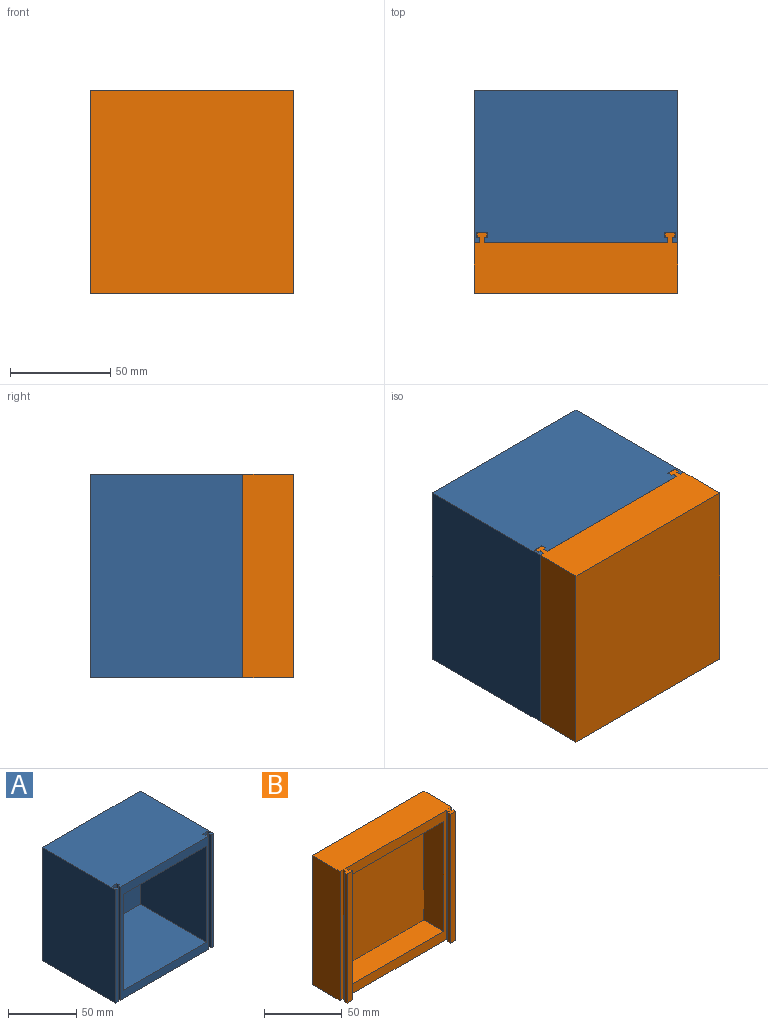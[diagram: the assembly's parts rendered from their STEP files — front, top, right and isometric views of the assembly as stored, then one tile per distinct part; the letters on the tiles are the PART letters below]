
ASSEMBLY  parts=2 mates=1
PART A: 27 faces, bbox 101.6x76.2x101.6 mm
  f0: plane 101.6x91.44mm, normal (0,-1,0), area 1832.3mm2, adj f2,f3,f8,f9,f10,f11,f13,f26
  f1: plane 101.6x2.54mm, normal (0,-1,0), area 258.1mm2, adj f2,f3,f5,f19
  f2: plane 101.6x76.2mm, normal (0,0,-1), area 7703.2mm2, adj f0,f1,f4,f5,f6,f7,f13,f14
  f3: plane 101.6x76.2mm, normal (0,0,1), area 7703.2mm2, adj f0,f1,f4,f5,f6,f7,f13,f14
  f4: plane 101.6x2.54mm, normal (0,-1,0), area 258.1mm2, adj f2,f3,f6,f20
  f5: plane 101.6x76.2mm, normal (1,0,0), area 7741.9mm2, adj f1,f2,f3,f7
  f6: plane 101.6x76.2mm, normal (-1,0,0), area 7741.9mm2, adj f2,f3,f4,f7
  f7: plane 101.6x101.6mm, normal (0,1,0), area 10322.6mm2, adj f2,f3,f5,f6
  f8: plane 86.36x68.58mm, normal (0,0,1), area 5922.6mm2, adj f0,f9,f11,f12
  f9: plane 86.36x68.58mm, normal (-1,0,0), area 5922.6mm2, adj f0,f8,f10,f12
  f10: plane 86.36x68.58mm, normal (0,0,-1), area 5922.6mm2, adj f0,f9,f11,f12
  f11: plane 86.36x68.58mm, normal (1,0,0), area 5922.6mm2, adj f0,f8,f10,f12
  f12: plane 86.36x86.36mm, normal (0,-1,0), area 7458mm2, adj f8,f9,f10,f11
  f13: plane 101.6x2.54mm, normal (1,0,0), area 258.1mm2, adj f0,f2,f3,f14
  f14: plane 101.6x1.27mm, normal (0,1,0), area 129mm2, adj f2,f3,f13,f15
  f15: plane 101.6x2.54mm, normal (1,0,0), area 258.1mm2, adj f2,f3,f14,f16
  f16: plane 101.6x5.08mm, normal (0,-1,0), area 516.1mm2, adj f2,f3,f15,f17
  f17: plane 101.6x2.54mm, normal (-1,0,0), area 258.1mm2, adj f2,f3,f16,f18
  f18: plane 101.6x1.27mm, normal (0,1,0), area 129mm2, adj f2,f3,f17,f19
  f19: plane 101.6x2.54mm, normal (-1,0,0), area 258.1mm2, adj f1,f2,f3,f18
  f20: plane 101.6x2.54mm, normal (1,0,0), area 258.1mm2, adj f2,f3,f4,f21
  f21: plane 101.6x1.27mm, normal (0,1,0), area 129mm2, adj f2,f3,f20,f22
  f22: plane 101.6x2.54mm, normal (1,0,0), area 258.1mm2, adj f2,f3,f21,f23
  f23: plane 101.6x5.08mm, normal (0,-1,0), area 516.1mm2, adj f2,f3,f22,f24
  f24: plane 101.6x2.54mm, normal (-1,0,0), area 258.1mm2, adj f2,f3,f23,f25
  f25: plane 101.6x1.27mm, normal (0,1,0), area 129mm2, adj f2,f3,f24,f26
  f26: plane 101.6x2.54mm, normal (-1,0,0), area 258.1mm2, adj f0,f2,f3,f25
PART B: 27 faces, bbox 101.6x30.4x101.6 mm
  f0: plane 101.6x2.67mm, normal (0,-1,0), area 271mm2, adj f3,f4,f5,f20
  f1: plane 101.6x91.69mm, normal (0,-1,0), area 1858.1mm2, adj f3,f5,f8,f9,f10,f11,f14,f26
  f2: plane 101.6x2.67mm, normal (0,-1,0), area 271mm2, adj f3,f5,f6,f13
  f3: plane 101.6x30.35mm, normal (0,0,-1), area 2614.9mm2, adj f0,f1,f2,f4,f6,f7,f13,f14
  f4: plane 101.6x25.4mm, normal (1,0,0), area 2580.6mm2, adj f0,f3,f5,f7
  f5: plane 101.6x30.35mm, normal (0,0,1), area 2614.9mm2, adj f0,f1,f2,f4,f6,f7,f13,f14
  f6: plane 101.6x25.4mm, normal (-1,0,0), area 2580.6mm2, adj f2,f3,f5,f7
  f7: plane 101.6x101.6mm, normal (0,1,0), area 10322.6mm2, adj f3,f4,f5,f6
  f8: plane 86.36x17.78mm, normal (0,0,1), area 1535.5mm2, adj f1,f9,f11,f12
  f9: plane 86.36x17.78mm, normal (-1,0,0), area 1535.5mm2, adj f1,f8,f10,f12
  f10: plane 86.36x17.78mm, normal (0,0,-1), area 1535.5mm2, adj f1,f9,f11,f12
  f11: plane 86.36x17.78mm, normal (1,0,0), area 1535.5mm2, adj f1,f8,f10,f12
  f12: plane 86.36x86.36mm, normal (0,-1,0), area 7458mm2, adj f8,f9,f10,f11
  f13: plane 101.6x2.67mm, normal (-1,0,0), area 271mm2, adj f2,f3,f5,f19
  f14: plane 101.6x2.67mm, normal (1,0,0), area 271mm2, adj f1,f3,f5,f15
  f15: plane 101.6x1.27mm, normal (0,1,0), area 129mm2, adj f3,f5,f14,f16
  f16: plane 101.6x2.29mm, normal (1,0,0), area 232.3mm2, adj f3,f5,f15,f17
  f17: plane 101.6x4.83mm, normal (0,-1,0), area 490.3mm2, adj f3,f5,f16,f18
  f18: plane 101.6x2.29mm, normal (-1,0,0), area 232.3mm2, adj f3,f5,f17,f19
  f19: plane 101.6x1.27mm, normal (0,1,0), area 129mm2, adj f3,f5,f13,f18
  f20: plane 101.6x2.67mm, normal (1,0,0), area 271mm2, adj f0,f3,f5,f21
  f21: plane 101.6x1.27mm, normal (0,1,0), area 129mm2, adj f3,f5,f20,f22
  f22: plane 101.6x2.29mm, normal (1,0,0), area 232.3mm2, adj f3,f5,f21,f23
  f23: plane 101.6x4.83mm, normal (0,-1,0), area 490.3mm2, adj f3,f5,f22,f24
  f24: plane 101.6x2.29mm, normal (-1,0,0), area 232.3mm2, adj f3,f5,f23,f25
  f25: plane 101.6x1.27mm, normal (0,1,0), area 129mm2, adj f3,f5,f24,f26
  f26: plane 101.6x2.67mm, normal (-1,0,0), area 271mm2, adj f1,f3,f5,f25
PLACE A t=(-4.29,-61.02,10.72)mm
PLACE B rot(axis=(0,0,1),180deg) t=(-4.29,-162.62,10.72)mm
MATE planar A.f0 <-> B.f1  axis (0,-1,0) through (-4.29,-137.22,10.72)mm
